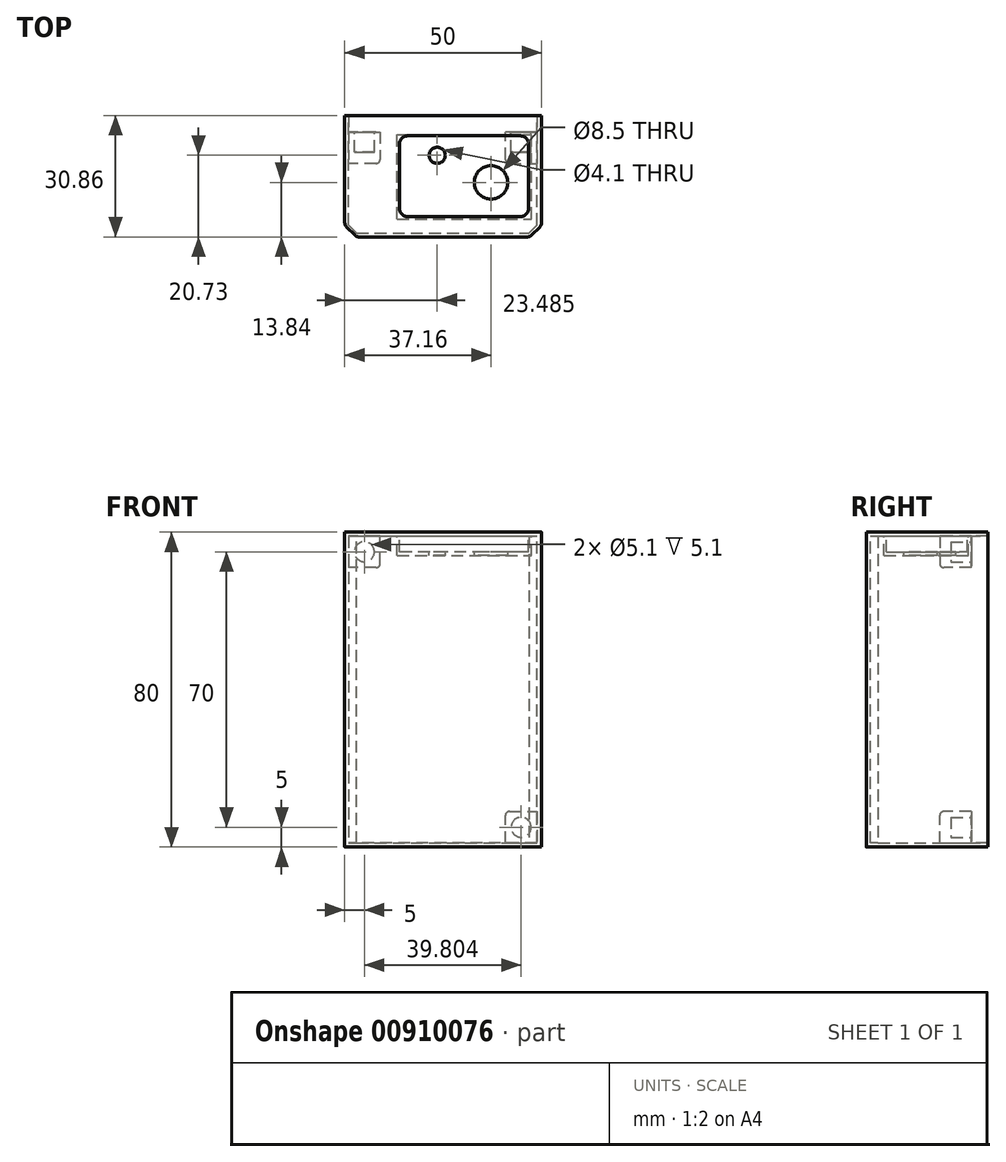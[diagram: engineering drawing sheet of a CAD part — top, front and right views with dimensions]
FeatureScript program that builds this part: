
annotation { "Feature Type Name" : "Feature", "Feature Type Description" : "" }
export const myFeature = defineFeature(function(context is Context, id is Id, definition is map)
    precondition{}
    {
        {
            var Q0;
            Q0=qCreatedBy(makeId("Top.planeOp"),FACE);
            var sketch = newSketch(context, id + "F0", { "sketchPlane" : qUnion([Q0])});
            skLineSegment(sketch, "E0.bottom", {"start": v(25, -13.84) * mm, "end": v(-25, -13.84) * mm});
            skLineSegment(sketch, "E0.top", {"start": v(25, 13.84) * mm, "end": v(-25, 13.84) * mm});
            skLineSegment(sketch, "E0.left", {"start": v(25, -13.84) * mm, "end": v(25, 13.84) * mm});
            skLineSegment(sketch, "E0.right", {"start": v(-25, -13.84) * mm, "end": v(-25, 13.84) * mm});
            skPoint(sketch, "E0.middle", {"position": v(0, 0) * mm});
            skCircle(sketch, "E1", {"center": v(12.16, 0) * mm, "radius": 4.25 * mm});
            skLineSegment(sketch, "E2.bottom", {"start": v(21.65, 8.66) * mm, "end": v(-11.1, 8.66) * mm});
            skLineSegment(sketch, "E2.top", {"start": v(21.66, -11.84) * mm, "end": v(-11.1, -11.84) * mm});
            skLineSegment(sketch, "E2.left", {"start": v(21.65, 8.66) * mm, "end": v(21.66, -11.84) * mm});
            skLineSegment(sketch, "E2.right", {"start": v(-11.1, 8.66) * mm, "end": v(-11.1, -11.84) * mm});
            skCircle(sketch, "E3", {"center": v(-1.52, -6.9) * mm, "radius": 2.05 * mm});
            skSolve(sketch);
        }
        {
            var Q0;
            Q0=makeQuery(id+"F0.imprint","IMPRINT",FACE,{"disambiguationData":[TD([[makeQuery(id+"F0.imprint","IMPRINT",EDGE,{"derivedFrom":sQuery(id+"F0.wireOp",EDGE,"E0.bottom")}),-1.0]])]});
            var sketch = newSketch(context, id + "F1", { "sketchPlane" : qUnion([Q0])});
            skLineSegment(sketch, "E4.bottom", {"start": v(-11.74, 9.3) * mm, "end": v(22.4, 9.3) * mm});
            skLineSegment(sketch, "E4.top", {"start": v(-11.74, -12.13) * mm, "end": v(22.4, -12.13) * mm});
            skLineSegment(sketch, "E4.left", {"start": v(-11.74, 9.3) * mm, "end": v(-11.74, -12.13) * mm});
            skLineSegment(sketch, "E4.right", {"start": v(22.4, 9.3) * mm, "end": v(22.4, -12.13) * mm});
            skLineSegment(sketch, "E5.bottom", {"start": v(-24, 12.84) * mm, "end": v(23.8, 12.84) * mm});
            skLineSegment(sketch, "E5.top", {"start": v(-24, -12.84) * mm, "end": v(23.8, -12.84) * mm});
            skLineSegment(sketch, "E5.left", {"start": v(-24, 12.84) * mm, "end": v(-24, -12.84) * mm});
            skLineSegment(sketch, "E5.right", {"start": v(23.8, 12.84) * mm, "end": v(23.8, -12.84) * mm});
            skSolve(sketch);
        }
        {
            var Q0;
            Q0=makeQuery(id+"F1.imprint","IMPRINT",FACE,{"disambiguationData":[TD([[makeQuery(id+"F1.imprint","IMPRINT",EDGE,{"derivedFrom":sQuery(id+"F1.wireOp",EDGE,"E5.bottom")}),1.0]])]});
            extrude(context, id + "F2", {"entities" : qUnion([Q0]), "depth" : 80 * mm, "offsetDistance" : 25 * mm});
        }
        {
            var Q0;
            Q0=makeQuery(id+"F1.imprint","IMPRINT",FACE,{"disambiguationData":[TD([[makeQuery(id+"F1.imprint","IMPRINT",EDGE,{"derivedFrom":sQuery(id+"F1.wireOp",EDGE,"E4.bottom")}),-1.0]])]});
            extrude(context, id + "F3", {"entities" : qUnion([Q0]), "depth" : 6 * mm, "offsetDistance" : 25 * mm});
        }
        {
            var Q0;
            Q0=makeQuery(id+"F0.imprint","IMPRINT",FACE,{"disambiguationData":[TD([[makeQuery(id+"F0.imprint","IMPRINT",EDGE,{"derivedFrom":sQuery(id+"F0.wireOp",EDGE,"E1")}),-1.0]])]});
            extrude(context, id + "F4", {"entities" : qUnion([Q0]), "operationType" : NewBodyOperationType.ADD, "depth" : 6 * mm, "offsetDistance" : 25 * mm});
        }
        {
            var Q0;
            Q0=makeQuery(id+"F1.imprint","IMPRINT",FACE,{"disambiguationData":[TD([[makeQuery(id+"F1.imprint","IMPRINT",EDGE,{"derivedFrom":makeQuery(id+"F0.imprint","IMPRINT",EDGE,{"derivedFrom":sQuery(id+"F0.wireOp",EDGE,"E2.bottom")})}),1.0]])]});
            extrude(context, id + "F5", {"entities" : qUnion([Q0]), "operationType" : NewBodyOperationType.REMOVE, "depth" : 5 * mm, "offsetDistance" : 25 * mm});
        }
        {
            var Q0;
            Q0=makeQuery(id+"F1.imprint","IMPRINT",FACE,{"disambiguationData":[TD([[makeQuery(id+"F1.imprint","IMPRINT",EDGE,{"derivedFrom":sQuery(id+"F1.wireOp",EDGE,"E4.bottom")}),1.0]])]});
            extrude(context, id + "F6", {"entities" : qUnion([Q0]), "depth" : 1 * mm, "offsetDistance" : 25 * mm});
        }
        {
            var Q0;
            Q0=makeQuery(id+"F5.boolean.opBoolean","COPY",EDGE,{"derivedFrom":makeQuery(id+"F5.opExtrude","SWEPT_EDGE",EDGE,{"disambiguationData":[OSD([sQuery(id+"F0.wireOp",EDGE,"E2.top"),sQuery(id+"F0.wireOp",EDGE,"E2.left")])]})});
            var Q1;
            Q1=makeQuery(id+"F5.boolean.opBoolean","COPY",EDGE,{"derivedFrom":makeQuery(id+"F5.opExtrude","SWEPT_EDGE",EDGE,{"disambiguationData":[OSD([sQuery(id+"F0.wireOp",EDGE,"E2.top"),sQuery(id+"F0.wireOp",EDGE,"E2.right")])]})});
            var Q2;
            Q2=makeQuery(id+"F5.boolean.opBoolean","COPY",EDGE,{"derivedFrom":makeQuery(id+"F5.opExtrude","SWEPT_EDGE",EDGE,{"disambiguationData":[OSD([sQuery(id+"F0.wireOp",EDGE,"E2.bottom"),sQuery(id+"F0.wireOp",EDGE,"E2.left")])]})});
            var Q3;
            Q3=makeQuery(id+"F5.boolean.opBoolean","COPY",EDGE,{"derivedFrom":makeQuery(id+"F5.opExtrude","SWEPT_EDGE",EDGE,{"disambiguationData":[OSD([sQuery(id+"F0.wireOp",EDGE,"E2.bottom"),sQuery(id+"F0.wireOp",EDGE,"E2.right")])]})});
            fillet(context, id + "F7", {"entities" : qUnion([Q0, Q1, Q2, Q3]), "radius" : 2 * mm, "tangentPropagation" : true, "allowEdgeOverflow" : false});
        }
        {
            var Q0;
            Q0=makeQuery(id+"F2.opExtrude","SWEPT_FACE",FACE,{"disambiguationData":[OSD([sQuery(id+"F0.wireOp",EDGE,"E0.bottom")])]});
            var sketch = newSketch(context, id + "F8", { "sketchPlane" : qUnion([Q0])});
            skLineSegment(sketch, "E6.bottom", {"start": v(25, 0) * mm, "end": v(-25, 0) * mm});
            skLineSegment(sketch, "E6.top", {"start": v(25, 80) * mm, "end": v(-25, 80) * mm});
            skLineSegment(sketch, "E6.left", {"start": v(25, 0) * mm, "end": v(25, 80) * mm});
            skLineSegment(sketch, "E6.right", {"start": v(-25, 0) * mm, "end": v(-25, 80) * mm});
            skSolve(sketch);
        }
        {
            var Q0;
            Q0=makeQuery(id+"F8.imprint","IMPRINT",FACE,{"disambiguationData":[TD([[makeQuery(id+"F8.imprint","IMPRINT",EDGE,{"derivedFrom":sQuery(id+"F8.wireOp",EDGE,"E6.bottom")}),-1.0]])]});
            extrude(context, id + "F9", {"entities" : qUnion([Q0]), "operationType" : NewBodyOperationType.REMOVE, "oppositeDirection" : true, "depth" : 1 * mm, "offsetDistance" : 25 * mm});
        }
        {
            var Q0;
            Q0=makeQuery(id+"F6.opExtrude","SWEPT_BODY",BODY,{"disambiguationData":[OSD([sQuery(id+"F1.wireOp",EDGE,"E4.bottom"),sQuery(id+"F1.wireOp",EDGE,"E4.top"),sQuery(id+"F1.wireOp",EDGE,"E4.left"),sQuery(id+"F1.wireOp",EDGE,"E4.right"),sQuery(id+"F1.wireOp",EDGE,"E5.bottom"),sQuery(id+"F1.wireOp",EDGE,"E5.top"),sQuery(id+"F1.wireOp",EDGE,"E5.left"),sQuery(id+"F1.wireOp",EDGE,"E5.right")])]});
            var Q1;
            Q1=makeQuery(id+"F2.opExtrude","SWEPT_BODY",BODY,{"disambiguationData":[OSD([sQuery(id+"F0.wireOp",EDGE,"E0.bottom"),sQuery(id+"F0.wireOp",EDGE,"E0.top"),sQuery(id+"F0.wireOp",EDGE,"E0.left"),sQuery(id+"F0.wireOp",EDGE,"E0.right"),sQuery(id+"F1.wireOp",EDGE,"E5.bottom"),sQuery(id+"F1.wireOp",EDGE,"E5.top"),sQuery(id+"F1.wireOp",EDGE,"E5.left"),sQuery(id+"F1.wireOp",EDGE,"E5.right")])]});
            var Q2;
            Q2=makeQuery(id+"F3.opExtrude","SWEPT_BODY",BODY,{"disambiguationData":[OSD([sQuery(id+"F0.wireOp",EDGE,"E2.bottom"),sQuery(id+"F0.wireOp",EDGE,"E2.top"),sQuery(id+"F0.wireOp",EDGE,"E2.left"),sQuery(id+"F0.wireOp",EDGE,"E2.right"),sQuery(id+"F1.wireOp",EDGE,"E4.bottom"),sQuery(id+"F1.wireOp",EDGE,"E4.top"),sQuery(id+"F1.wireOp",EDGE,"E4.left"),sQuery(id+"F1.wireOp",EDGE,"E4.right")])]});
            var Q3;
            Q3=makeQuery(id+"F6.opExtrude","CAP_EDGE",EDGE,{"disambiguationData":[OSD([sQuery(id+"F1.wireOp",EDGE,"E5.top")])],"isStart":true});
            transform(context, id + "F10", {"entities" : qUnion([Q0, Q1, Q2]), "transformType" : TransformType.ROTATION, "transformAxis" : qUnion([Q3]), "angle" : 180 * degree, "makeCopy" : false});
        }
        {
            var Q0;
            Q0=makeQuery(id+"F2.opExtrude","CAP_FACE",FACE,{"disambiguationData":[OSD([sQuery(id+"F0.wireOp",EDGE,"E0.bottom"),sQuery(id+"F0.wireOp",EDGE,"E0.top"),sQuery(id+"F0.wireOp",EDGE,"E0.left"),sQuery(id+"F0.wireOp",EDGE,"E0.right"),sQuery(id+"F1.wireOp",EDGE,"E5.bottom"),sQuery(id+"F1.wireOp",EDGE,"E5.top"),sQuery(id+"F1.wireOp",EDGE,"E5.left"),sQuery(id+"F1.wireOp",EDGE,"E5.right")])],"isStart":false});
            var sketch = newSketch(context, id + "F11", { "sketchPlane" : qUnion([Q0])});
            skLineSegment(sketch, "E7.bottom", {"start": v(23.8, 12.84) * mm, "end": v(-24, 12.84) * mm});
            skLineSegment(sketch, "E7.top", {"start": v(23.8, 38.52) * mm, "end": v(-24, 38.52) * mm});
            skLineSegment(sketch, "E7.left", {"start": v(23.8, 12.84) * mm, "end": v(23.8, 38.52) * mm});
            skLineSegment(sketch, "E7.right", {"start": v(-24, 12.84) * mm, "end": v(-24, 38.52) * mm});
            skSolve(sketch);
        }
        {
            var Q0;
            Q0=makeQuery(id+"F11.imprint","IMPRINT",FACE,{"disambiguationData":[TD([[makeQuery(id+"F11.imprint","IMPRINT",EDGE,{"derivedFrom":sQuery(id+"F11.wireOp",EDGE,"E7.bottom")}),-1.0]])]});
            extrude(context, id + "F12", {"entities" : qUnion([Q0]), "operationType" : NewBodyOperationType.ADD, "oppositeDirection" : true, "depth" : 1 * mm, "offsetDistance" : 25 * mm});
        }
        {
            var Q0;
            Q0=makeQuery(id+"F2.opExtrude","SWEPT_FACE",FACE,{"disambiguationData":[OSD([sQuery(id+"F1.wireOp",EDGE,"E5.left")])]});
            var sketch = newSketch(context, id + "F13", { "sketchPlane" : qUnion([Q0])});
            skLineSegment(sketch, "E8.bottom", {"start": v(-12.84, -1) * mm, "end": v(-20.84, -1) * mm});
            skLineSegment(sketch, "E8.top", {"start": v(-12.84, -9) * mm, "end": v(-20.84, -9) * mm});
            skLineSegment(sketch, "E8.left", {"start": v(-12.84, -1) * mm, "end": v(-12.84, -9) * mm});
            skLineSegment(sketch, "E8.right", {"start": v(-20.84, -1) * mm, "end": v(-20.84, -9) * mm});
            skSolve(sketch);
        }
        {
            var Q0;
            Q0=makeQuery(id+"F13.imprint","IMPRINT",FACE,{"disambiguationData":[TD([[makeQuery(id+"F13.imprint","IMPRINT",EDGE,{"derivedFrom":sQuery(id+"F13.wireOp",EDGE,"E8.bottom")}),1.0]])]});
            extrude(context, id + "F14", {"entities" : qUnion([Q0]), "depth" : 8 * mm, "offsetDistance" : 25 * mm});
        }
        {
            var Q0;
            Q0=makeQuery(id+"F2.opExtrude","SWEPT_FACE",FACE,{"disambiguationData":[OSD([sQuery(id+"F1.wireOp",EDGE,"E5.right")])]});
            var sketch = newSketch(context, id + "F15", { "sketchPlane" : qUnion([Q0])});
            skLineSegment(sketch, "E9.bottom", {"start": v(12.84, -79) * mm, "end": v(20.84, -79) * mm});
            skLineSegment(sketch, "E9.top", {"start": v(12.84, -71) * mm, "end": v(20.84, -71) * mm});
            skLineSegment(sketch, "E9.left", {"start": v(12.84, -79) * mm, "end": v(12.84, -71) * mm});
            skLineSegment(sketch, "E9.right", {"start": v(20.84, -79) * mm, "end": v(20.84, -71) * mm});
            skSolve(sketch);
        }
        {
            var Q0;
            Q0=makeQuery(id+"F15.imprint","IMPRINT",FACE,{"disambiguationData":[TD([[makeQuery(id+"F15.imprint","IMPRINT",EDGE,{"derivedFrom":sQuery(id+"F15.wireOp",EDGE,"E9.bottom")}),-1.0]])]});
            extrude(context, id + "F16", {"entities" : qUnion([Q0]), "operationType" : NewBodyOperationType.ADD, "depth" : 8 * mm, "offsetDistance" : 25 * mm});
        }
        {
            var Q0;
            Q0=makeQuery(id+"F14.opExtrude","SWEPT_BODY",BODY,{"disambiguationData":[OSD([sQuery(id+"F13.wireOp",EDGE,"E8.bottom"),sQuery(id+"F13.wireOp",EDGE,"E8.top"),sQuery(id+"F13.wireOp",EDGE,"E8.left"),sQuery(id+"F13.wireOp",EDGE,"E8.right")])]});
            var Q1;
            Q1=makeQuery(id+"F2.opExtrude","SWEPT_BODY",BODY,{"disambiguationData":[OSD([sQuery(id+"F0.wireOp",EDGE,"E0.bottom"),sQuery(id+"F0.wireOp",EDGE,"E0.top"),sQuery(id+"F0.wireOp",EDGE,"E0.left"),sQuery(id+"F0.wireOp",EDGE,"E0.right"),sQuery(id+"F1.wireOp",EDGE,"E5.bottom"),sQuery(id+"F1.wireOp",EDGE,"E5.top"),sQuery(id+"F1.wireOp",EDGE,"E5.left"),sQuery(id+"F1.wireOp",EDGE,"E5.right")])]});
            var Q2;
            Q2=makeQuery(id+"F3.opExtrude","SWEPT_BODY",BODY,{"disambiguationData":[OSD([sQuery(id+"F0.wireOp",EDGE,"E2.bottom"),sQuery(id+"F0.wireOp",EDGE,"E2.top"),sQuery(id+"F0.wireOp",EDGE,"E2.left"),sQuery(id+"F0.wireOp",EDGE,"E2.right"),sQuery(id+"F1.wireOp",EDGE,"E4.bottom"),sQuery(id+"F1.wireOp",EDGE,"E4.top"),sQuery(id+"F1.wireOp",EDGE,"E4.left"),sQuery(id+"F1.wireOp",EDGE,"E4.right")])]});
            var Q3;
            Q3=makeQuery(id+"F6.opExtrude","SWEPT_BODY",BODY,{"disambiguationData":[OSD([sQuery(id+"F1.wireOp",EDGE,"E4.bottom"),sQuery(id+"F1.wireOp",EDGE,"E4.top"),sQuery(id+"F1.wireOp",EDGE,"E4.left"),sQuery(id+"F1.wireOp",EDGE,"E4.right"),sQuery(id+"F1.wireOp",EDGE,"E5.bottom"),sQuery(id+"F1.wireOp",EDGE,"E5.top"),sQuery(id+"F1.wireOp",EDGE,"E5.left"),sQuery(id+"F1.wireOp",EDGE,"E5.right")])]});
            booleanBodies(context, id + "F17", {"operationType" : BooleanOperationType.UNION, "tools" : qUnion([Q0, Q1, Q2, Q3])});
        }
        {
            var Q0;
            {var subQ0=sQuery(id+"F1.wireOp",EDGE,"E5.right");var subQ1=sQuery(id+"F1.wireOp",EDGE,"E5.left");var subQ2=sQuery(id+"F1.wireOp",EDGE,"E5.top");var subQ10=makeQuery(id+"F9.opExtrude","CAP_FACE",FACE,{"disambiguationData":[OSD([sQuery(id+"F8.wireOp",EDGE,"E6.bottom"),sQuery(id+"F8.wireOp",EDGE,"E6.top"),sQuery(id+"F8.wireOp",EDGE,"E6.left"),sQuery(id+"F8.wireOp",EDGE,"E6.right")])],"isStart":false});Q0=makeQuery(id+"F17.opBoolean","MERGE",FACE,{"derivedFrom":[makeQuery(id+"F6.opExtrude","SWEPT_FACE",FACE,{"disambiguationData":[OSD([subQ2])]}),makeQuery(id+"F14.opExtrude","SWEPT_FACE",FACE,{"disambiguationData":[OSD([sQuery(id+"F13.wireOp",EDGE,"E8.left")])]}),makeQuery(id+"F16.boolean.opBoolean","MERGE",FACE,{"derivedFrom":[makeQuery(id+"F12.boolean.opBoolean","MERGE",FACE,{"derivedFrom":[makeQuery(id+"F9.boolean.opBoolean","COPY",FACE,{"disambiguationData":[TD([makeQuery(id+"F2.opExtrude","SWEPT_FACE",FACE,{"disambiguationData":[OSD([subQ0])]})])],"derivedFrom":subQ10}),makeQuery(id+"F9.boolean.opBoolean","COPY",FACE,{"disambiguationData":[TD([makeQuery(id+"F2.opExtrude","SWEPT_FACE",FACE,{"disambiguationData":[OSD([subQ1])]})])],"derivedFrom":subQ10}),makeQuery(id+"F12.opExtrude","SWEPT_FACE",FACE,{"disambiguationData":[OSD([sQuery(id+"F11.wireOp",EDGE,"E7.bottom")])]})]}),makeQuery(id+"F16.opExtrude","SWEPT_FACE",FACE,{"disambiguationData":[OSD([sQuery(id+"F15.wireOp",EDGE,"E9.left")])]})]})]});}
            var sketch = newSketch(context, id + "F18", { "sketchPlane" : qUnion([Q0])});
            skLineSegment(sketch, "E10", {"start": v(16, -5) * mm, "end": v(25, -5) * mm, "construction": true});
            skLineSegment(sketch, "E11", {"start": v(20, -9) * mm, "end": v(20, -1) * mm, "construction": true});
            skCircle(sketch, "E12", {"center": v(20, -5) * mm, "radius": 2.55 * mm});
            skCircle(sketch, "E13", {"center": v(-19.8, -75) * mm, "radius": 2.55 * mm});
            skSolve(sketch);
        }
        {
            var Q0;
            Q0=makeQuery(id+"F2.opExtrude","SWEPT_EDGE",EDGE,{"disambiguationData":[OSD([sQuery(id+"F1.wireOp",EDGE,"E5.bottom"),sQuery(id+"F1.wireOp",EDGE,"E5.right")])]});
            var Q1;
            Q1=makeQuery(id+"F2.opExtrude","SWEPT_EDGE",EDGE,{"disambiguationData":[OSD([sQuery(id+"F1.wireOp",EDGE,"E5.bottom"),sQuery(id+"F1.wireOp",EDGE,"E5.left")])]});
            chamfer(context, id + "F19", {"entities" : qUnion([Q0, Q1]), "width" : 2 * mm, "tangentPropagation" : true});
        }
        {
            var Q0;
            Q0=makeQuery(id+"F2.opExtrude","SWEPT_EDGE",EDGE,{"disambiguationData":[OSD([sQuery(id+"F0.wireOp",EDGE,"E0.top"),sQuery(id+"F0.wireOp",EDGE,"E0.left")])]});
            var Q1;
            Q1=makeQuery(id+"F2.opExtrude","SWEPT_EDGE",EDGE,{"disambiguationData":[OSD([sQuery(id+"F0.wireOp",EDGE,"E0.top"),sQuery(id+"F0.wireOp",EDGE,"E0.right")])]});
            chamfer(context, id + "F20", {"entities" : qUnion([Q0, Q1]), "width" : 3 * mm, "tangentPropagation" : true});
        }
        {
            var Q0;
            {var subQ0=sQuery(id+"F0.wireOp",EDGE,"E0.left");Q0=makeQuery(id+"F20.opChamfer","BLEND_EDGE",EDGE,{"blendedFrom":[makeQuery(id+"F2.opExtrude","SWEPT_EDGE",EDGE,{"disambiguationData":[OSD([sQuery(id+"F0.wireOp",EDGE,"E0.top"),subQ0])]}),makeQuery(id+"F2.opExtrude","SWEPT_FACE",FACE,{"disambiguationData":[OSD([subQ0])]})],"blendedInto":[makeQuery(id+"F2.opExtrude","SWEPT_FACE",FACE,{"disambiguationData":[OSD([subQ0])]})]});}
            var Q1;
            {var subQ0=sQuery(id+"F0.wireOp",EDGE,"E0.top");Q1=makeQuery(id+"F20.opChamfer","BLEND_EDGE",EDGE,{"blendedFrom":[makeQuery(id+"F2.opExtrude","SWEPT_EDGE",EDGE,{"disambiguationData":[OSD([subQ0,sQuery(id+"F0.wireOp",EDGE,"E0.left")])]}),makeQuery(id+"F2.opExtrude","SWEPT_FACE",FACE,{"disambiguationData":[OSD([subQ0])]})],"blendedInto":[makeQuery(id+"F2.opExtrude","SWEPT_FACE",FACE,{"disambiguationData":[OSD([subQ0])]})]});}
            var Q2;
            {var subQ0=sQuery(id+"F0.wireOp",EDGE,"E0.right");Q2=makeQuery(id+"F20.opChamfer","BLEND_EDGE",EDGE,{"blendedFrom":[makeQuery(id+"F2.opExtrude","SWEPT_EDGE",EDGE,{"disambiguationData":[OSD([sQuery(id+"F0.wireOp",EDGE,"E0.top"),subQ0])]}),makeQuery(id+"F2.opExtrude","SWEPT_FACE",FACE,{"disambiguationData":[OSD([subQ0])]})],"blendedInto":[makeQuery(id+"F2.opExtrude","SWEPT_FACE",FACE,{"disambiguationData":[OSD([subQ0])]})]});}
            var Q3;
            {var subQ0=sQuery(id+"F0.wireOp",EDGE,"E0.top");Q3=makeQuery(id+"F20.opChamfer","BLEND_EDGE",EDGE,{"blendedFrom":[makeQuery(id+"F2.opExtrude","SWEPT_EDGE",EDGE,{"disambiguationData":[OSD([subQ0,sQuery(id+"F0.wireOp",EDGE,"E0.right")])]}),makeQuery(id+"F2.opExtrude","SWEPT_FACE",FACE,{"disambiguationData":[OSD([subQ0])]})],"blendedInto":[makeQuery(id+"F2.opExtrude","SWEPT_FACE",FACE,{"disambiguationData":[OSD([subQ0])]})]});}
            fillet(context, id + "F21", {"entities" : qUnion([Q0, Q1, Q2, Q3]), "radius" : 1.5 * mm, "tangentPropagation" : true, "allowEdgeOverflow" : false});
        }
        {
            var Q0;
            Q0=makeQuery(id+"F14.opExtrude","CAP_EDGE",EDGE,{"disambiguationData":[OSD([sQuery(id+"F13.wireOp",EDGE,"E8.top")])],"isStart":true});
            var Q1;
            Q1=makeQuery(id+"F14.opExtrude","SWEPT_EDGE",EDGE,{"disambiguationData":[OSD([sQuery(id+"F13.wireOp",EDGE,"E8.top"),sQuery(id+"F13.wireOp",EDGE,"E8.right")])]});
            var Q2;
            Q2=makeQuery(id+"F14.opExtrude","CAP_EDGE",EDGE,{"disambiguationData":[OSD([sQuery(id+"F13.wireOp",EDGE,"E8.top")])],"isStart":false});
            var Q3;
            Q3=makeQuery(id+"F14.opExtrude","CAP_EDGE",EDGE,{"disambiguationData":[OSD([sQuery(id+"F13.wireOp",EDGE,"E8.right")])],"isStart":false});
            var Q4;
            Q4=makeQuery(id+"F14.opExtrude","CAP_EDGE",EDGE,{"disambiguationData":[OSD([sQuery(id+"F13.wireOp",EDGE,"E8.bottom")])],"isStart":false});
            var Q5;
            Q5=makeQuery(id+"F16.opExtrude","CAP_EDGE",EDGE,{"disambiguationData":[OSD([sQuery(id+"F15.wireOp",EDGE,"E9.top")])],"isStart":false});
            var Q6;
            Q6=makeQuery(id+"F16.opExtrude","CAP_EDGE",EDGE,{"disambiguationData":[OSD([sQuery(id+"F15.wireOp",EDGE,"E9.top")])],"isStart":true});
            var Q7;
            Q7=makeQuery(id+"F16.opExtrude","CAP_EDGE",EDGE,{"disambiguationData":[OSD([sQuery(id+"F15.wireOp",EDGE,"E9.bottom")])],"isStart":false});
            var Q8;
            Q8=makeQuery(id+"F16.opExtrude","CAP_EDGE",EDGE,{"disambiguationData":[OSD([sQuery(id+"F15.wireOp",EDGE,"E9.right")])],"isStart":false});
            var Q9;
            Q9=makeQuery(id+"F16.opExtrude","SWEPT_EDGE",EDGE,{"disambiguationData":[OSD([sQuery(id+"F15.wireOp",EDGE,"E9.top"),sQuery(id+"F15.wireOp",EDGE,"E9.right")])]});
            var Q10;
            Q10=makeQuery(id+"F6.opExtrude","CAP_EDGE",EDGE,{"disambiguationData":[OSD([sQuery(id+"F1.wireOp",EDGE,"E4.left")])],"isStart":false});
            var Q11;
            Q11=makeQuery(id+"F6.opExtrude","CAP_EDGE",EDGE,{"disambiguationData":[OSD([sQuery(id+"F1.wireOp",EDGE,"E4.right")])],"isStart":false});
            fillet(context, id + "F22", {"entities" : qUnion([Q0, Q1, Q2, Q3, Q4, Q5, Q6, Q7, Q8, Q9, Q10, Q11]), "radius" : 1 * mm, "tangentPropagation" : true, "allowEdgeOverflow" : false});
        }
        {
            var Q0;
            Q0=makeQuery(id+"F18.imprint","IMPRINT",FACE,{"disambiguationData":[TD([[makeQuery(id+"F18.imprint","IMPRINT",EDGE,{"derivedFrom":sQuery(id+"F18.wireOp",EDGE,"E12")}),1.0]])]});
            var Q1;
            Q1=makeQuery(id+"F18.imprint","IMPRINT",FACE,{"disambiguationData":[TD([[makeQuery(id+"F18.imprint","IMPRINT",EDGE,{"derivedFrom":sQuery(id+"F18.wireOp",EDGE,"E13")}),1.0]])]});
            extrude(context, id + "F23", {"entities" : qUnion([Q0, Q1]), "operationType" : NewBodyOperationType.REMOVE, "oppositeDirection" : true, "depth" : 5.1 * mm, "offsetDistance" : 25 * mm});
        }
        {
            var Q0;
            {var subQ0=sQuery(id+"F1.wireOp",EDGE,"E5.right");var subQ1=sQuery(id+"F1.wireOp",EDGE,"E5.left");var subQ2=sQuery(id+"F1.wireOp",EDGE,"E5.top");var subQ10=makeQuery(id+"F9.opExtrude","CAP_FACE",FACE,{"disambiguationData":[OSD([sQuery(id+"F8.wireOp",EDGE,"E6.bottom"),sQuery(id+"F8.wireOp",EDGE,"E6.top"),sQuery(id+"F8.wireOp",EDGE,"E6.left"),sQuery(id+"F8.wireOp",EDGE,"E6.right")])],"isStart":false});Q0=makeQuery(id+"F17.opBoolean","MERGE",FACE,{"derivedFrom":[makeQuery(id+"F6.opExtrude","SWEPT_FACE",FACE,{"disambiguationData":[OSD([subQ2])]}),makeQuery(id+"F14.opExtrude","SWEPT_FACE",FACE,{"disambiguationData":[OSD([sQuery(id+"F13.wireOp",EDGE,"E8.left")])]}),makeQuery(id+"F16.boolean.opBoolean","MERGE",FACE,{"derivedFrom":[makeQuery(id+"F12.boolean.opBoolean","MERGE",FACE,{"derivedFrom":[makeQuery(id+"F9.boolean.opBoolean","COPY",FACE,{"disambiguationData":[TD([makeQuery(id+"F2.opExtrude","SWEPT_FACE",FACE,{"disambiguationData":[OSD([subQ0])]})])],"derivedFrom":subQ10}),makeQuery(id+"F9.boolean.opBoolean","COPY",FACE,{"disambiguationData":[TD([makeQuery(id+"F2.opExtrude","SWEPT_FACE",FACE,{"disambiguationData":[OSD([subQ1])]})])],"derivedFrom":subQ10}),makeQuery(id+"F12.opExtrude","SWEPT_FACE",FACE,{"disambiguationData":[OSD([sQuery(id+"F11.wireOp",EDGE,"E7.bottom")])]})]}),makeQuery(id+"F16.opExtrude","SWEPT_FACE",FACE,{"disambiguationData":[OSD([sQuery(id+"F15.wireOp",EDGE,"E9.left")])]})]})]});}
            var sketch = newSketch(context, id + "F24", { "sketchPlane" : qUnion([Q0])});
            skLineSegment(sketch, "E14.bottom", {"start": v(-25, 0) * mm, "end": v(25, 0) * mm});
            skLineSegment(sketch, "E14.top", {"start": v(-25, -80) * mm, "end": v(25, -80) * mm});
            skLineSegment(sketch, "E14.left", {"start": v(-25, 0) * mm, "end": v(-25, -80) * mm});
            skLineSegment(sketch, "E14.right", {"start": v(25, 0) * mm, "end": v(25, -80) * mm});
            skLineSegment(sketch, "E15.bottom", {"start": v(-23.8, -1) * mm, "end": v(24, -1) * mm});
            skLineSegment(sketch, "E15.top", {"start": v(-23.8, -79) * mm, "end": v(24, -79) * mm});
            skLineSegment(sketch, "E15.left", {"start": v(-23.8, -1) * mm, "end": v(-23.8, -79) * mm});
            skLineSegment(sketch, "E15.right", {"start": v(24, -1) * mm, "end": v(24, -79) * mm});
            skSolve(sketch);
        }
        {
            var Q0;
            Q0=makeQuery(id+"F24.imprint","IMPRINT",FACE,{"disambiguationData":[TD([[makeQuery(id+"F24.imprint","IMPRINT",EDGE,{"derivedFrom":sQuery(id+"F24.wireOp",EDGE,"E14.bottom")}),-1.0]])]});
            extrude(context, id + "F25", {"entities" : qUnion([Q0]), "operationType" : NewBodyOperationType.ADD, "depth" : 4.18 * mm, "offsetDistance" : 25 * mm});
        }
    });
